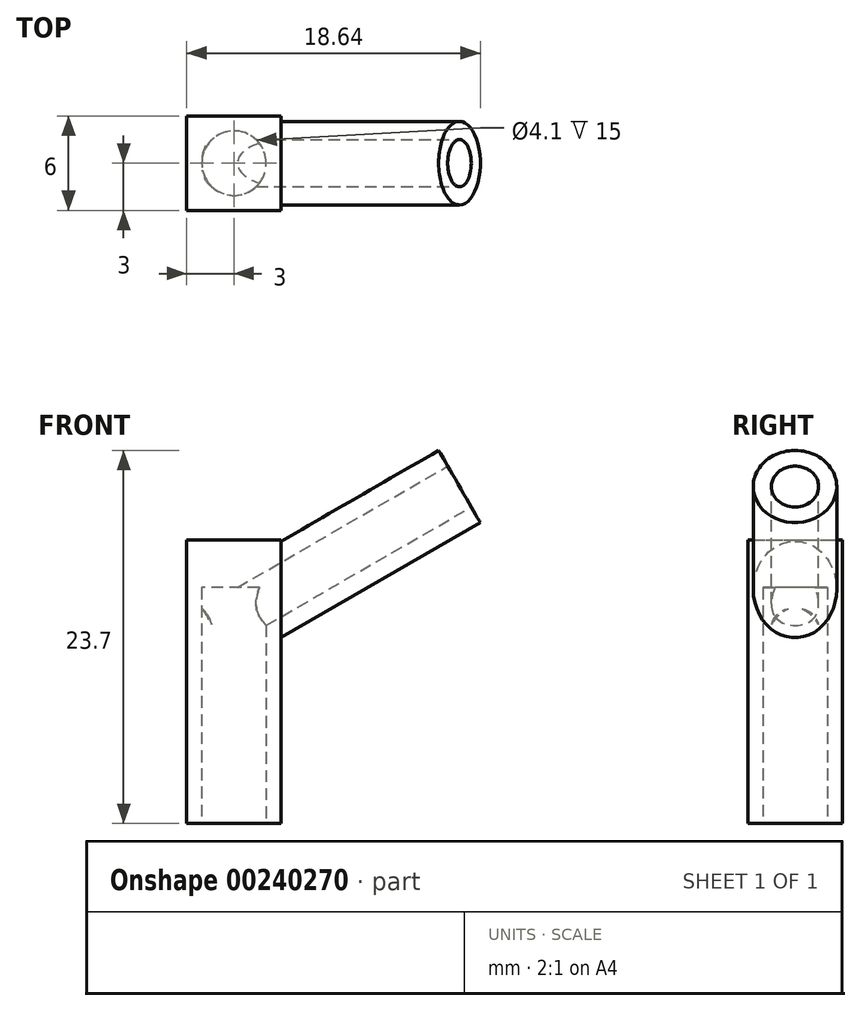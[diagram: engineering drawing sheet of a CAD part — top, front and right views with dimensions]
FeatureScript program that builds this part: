
annotation { "Feature Type Name" : "Feature", "Feature Type Description" : "" }
export const myFeature = defineFeature(function(context is Context, id is Id, definition is map)
    precondition{}
    {
        {
            var Q0;
            Q0=qCreatedBy(makeId("Top.planeOp"),FACE);
            var sketch = newSketch(context, id + "F0", { "sketchPlane" : qUnion([Q0])});
            skCircle(sketch, "E0", {"center": v(0, 0) * mm, "radius": 2.05 * mm});
            skLineSegment(sketch, "E1.bottom", {"start": v(3, -3) * mm, "end": v(-3, -3) * mm});
            skLineSegment(sketch, "E1.top", {"start": v(3, 3) * mm, "end": v(-3, 3) * mm});
            skLineSegment(sketch, "E1.left", {"start": v(3, -3) * mm, "end": v(3, 3) * mm});
            skLineSegment(sketch, "E1.right", {"start": v(-3, -3) * mm, "end": v(-3, 3) * mm});
            skSolve(sketch);
        }
        {
            var Q0;
            Q0 = qSketchRegion(id + "F0", true);
            extrude(context, id + "F1", {"entities" : qUnion([Q0]), "depth" : 15 * mm});
        }
        {
            var Q0;
            Q0=makeQuery(id+"F1.opExtrude","CAP_FACE",FACE,{"disambiguationData":[OSD([sQuery(id+"F0.wireOp",EDGE,"E0"),sQuery(id+"F0.wireOp",EDGE,"E1.bottom"),sQuery(id+"F0.wireOp",EDGE,"E1.top"),sQuery(id+"F0.wireOp",EDGE,"E1.left"),sQuery(id+"F0.wireOp",EDGE,"E1.right")])],"isStart":false});
            cPlane(context, id + "F2", {"entities" : qUnion([Q0]), "cplaneType" : CPlaneType.OFFSET, "offset" : 0 * mm, "width" : 150 * mm, "height" : 150 * mm});
        }
        {
            var Q0;
            Q0=qCreatedBy(id+"F2.planeOp",FACE);
            var sketch = newSketch(context, id + "F3", { "sketchPlane" : qUnion([Q0])});
            skLineSegment(sketch, "E2.0", {"start": v(-3, -3) * mm, "end": v(-3, 3) * mm});
            skLineSegment(sketch, "E3.0.0", {"start": v(3, -3) * mm, "end": v(3, 3) * mm});
            skLineSegment(sketch, "E3.0.1", {"start": v(3, 3) * mm, "end": v(-3, 3) * mm});
            skLineSegment(sketch, "E3.0.2", {"start": v(-3, 3) * mm, "end": v(-3, -3) * mm});
            skLineSegment(sketch, "E3.0.3", {"start": v(-3, -3) * mm, "end": v(3, -3) * mm});
            skSolve(sketch);
        }
        {
            var Q0;
            Q0 = qSketchRegion(id + "F3", true);
            extrude(context, id + "F4", {"entities" : qUnion([Q0]), "operationType" : NewBodyOperationType.ADD, "depth" : 3 * mm});
        }
        {
            var Q0;
            Q0=qCreatedBy(makeId("Front.planeOp"),FACE);
            var sketch = newSketch(context, id + "F5", { "sketchPlane" : qUnion([Q0])});
            skLineSegment(sketch, "E4", {"start": v(3.88, 19.5) * mm, "end": v(7.1, 13.93) * mm});
            skSolve(sketch);
        }
        {
            var Q0;
            Q0 = qConstructionFilter(qBodyType(qCreatedBy(id + "F5" ,EDGE), BodyType.WIRE), ConstructionObject.NO);
            extrude(context, id + "F6", {"bodyType" : ToolBodyType.SURFACE, "surfaceEntities" : qUnion([Q0]), "endBound" : BoundingType.SYMMETRIC, "depth" : 25 * mm});
        }
        {
            var Q0;
            Q0=makeQuery(id+"F6.opExtrude","SWEPT_FACE",FACE,{"disambiguationData":[OSD([sQuery(id+"F5.wireOp",EDGE,"E4")])]});
            cPlane(context, id + "F7", {"entities" : qUnion([Q0]), "cplaneType" : CPlaneType.OFFSET, "offset" : 0 * mm, "width" : 150 * mm, "height" : 150 * mm});
        }
        {
            var Q0;
            Q0=qCreatedBy(id+"F7.planeOp",FACE);
            var sketch = newSketch(context, id + "F8", { "sketchPlane" : qUnion([Q0])});
            skCircle(sketch, "E5", {"center": v(0, 11.38) * mm, "radius": 2.65 * mm});
            skCircle(sketch, "E6.0", {"center": v(0, 11.38) * mm, "radius": 1.5 * mm});
            skSolve(sketch);
        }
        {
            var Q0;
            Q0 = qSketchRegion(id + "F8", true);
            var Q1;
            Q1=makeQuery(id+"F4.boolean.opBoolean","MERGE",FACE,{"derivedFrom":[makeQuery(id+"F1.opExtrude","SWEPT_FACE",FACE,{"disambiguationData":[OSD([sQuery(id+"F0.wireOp",EDGE,"E1.left")])]}),makeQuery(id+"F4.opExtrude","SWEPT_FACE",FACE,{"disambiguationData":[OSD([sQuery(id+"F3.wireOp",EDGE,"E3.0.0")])]})]});
            extrude(context, id + "F9", {"entities" : qUnion([Q0]), "operationType" : NewBodyOperationType.ADD, "endBound" : BoundingType.UP_TO_SURFACE, "endBoundEntityFace" : qUnion([Q1]), "depth" : 25 * mm});
        }
        {
            var Q0;
            Q0 = qSketchRegion(id + "F8", true);
            extrude(context, id + "F10", {"entities" : qUnion([Q0]), "operationType" : NewBodyOperationType.ADD, "oppositeDirection" : true, "depth" : 10 * mm});
        }
        {
            var Q0;
            Q0=makeQuery(id+"F8.imprint","IMPRINT",FACE,{"disambiguationData":[TD([[makeQuery(id+"F8.imprint","IMPRINT",EDGE,{"derivedFrom":sQuery(id+"F8.wireOp",EDGE,"E6.0")}),1.0]])]});
            extrude(context, id + "F11", {"entities" : qUnion([Q0]), "operationType" : NewBodyOperationType.REMOVE, "depth" : 8.02 * mm});
        }
    });
